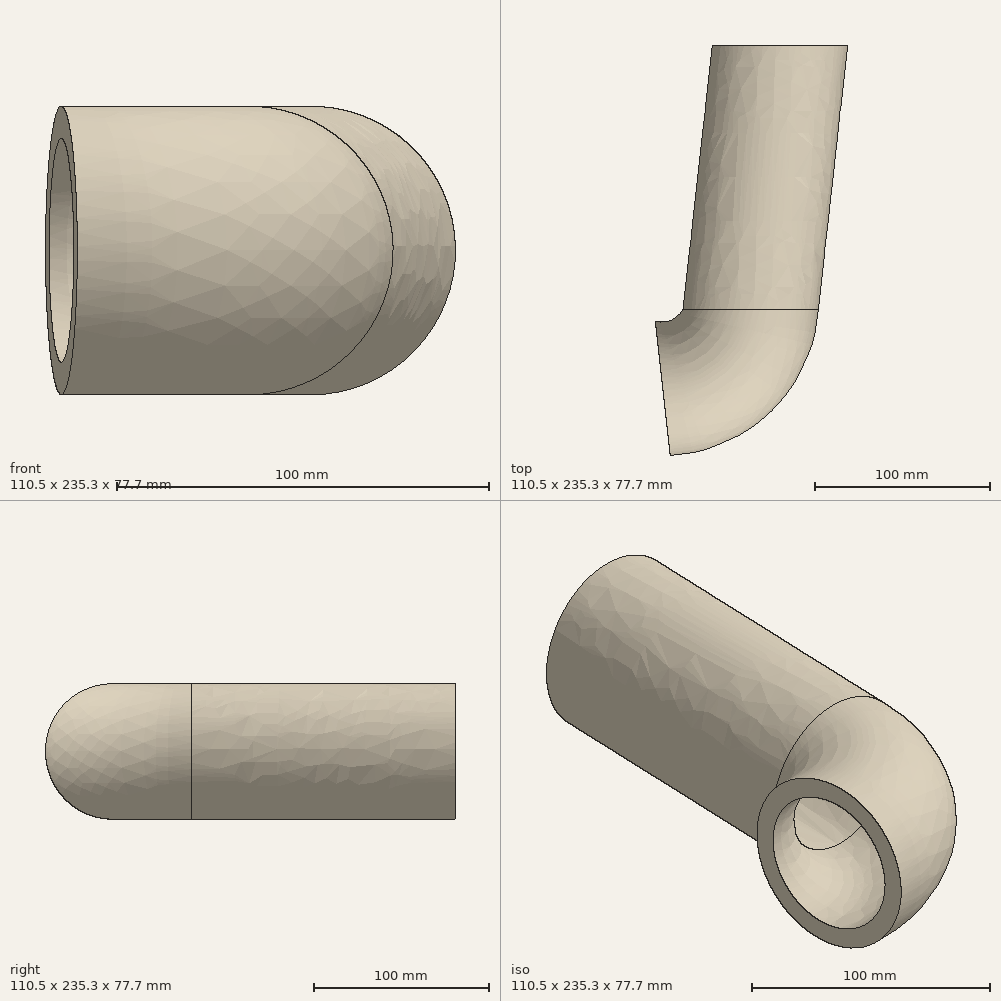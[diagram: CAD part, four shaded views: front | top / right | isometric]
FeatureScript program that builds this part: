
annotation { "Feature Type Name" : "Feature", "Feature Type Description" : "" }
export const myFeature = defineFeature(function(context is Context, id is Id, definition is map)
    precondition{}
    {
        {
            var Q0;
            Q0=qCreatedBy(makeId("Front.planeOp"),FACE);
            var sketch = newSketch(context, id + "F0", { "sketchPlane" : qUnion([Q0])});
            skCircle(sketch, "E0", {"center": v(0, 0) * mm, "radius": 30.16 * mm});
            skCircle(sketch, "E1.0", {"center": v(0, 0) * mm, "radius": 38.87 * mm});
            skSolve(sketch);
        }
        {
            var Q0;
            Q0=qCreatedBy(makeId("Top.planeOp"),FACE);
            var sketch = newSketch(context, id + "F1", { "sketchPlane" : qUnion([Q0])});
            skLineSegment(sketch, "E2", {"start": v(0, 0) * mm, "end": v(-16.82, -151.47) * mm});
            skLineSegment(sketch, "E3", {"start": v(-16.82, -151.47) * mm, "end": v(-67.3, -145.86) * mm, "construction": true});
            skArc(sketch, "E4", {"start": v(-16.82, -151.47) * mm, "mid": v(-33.42, -183.71) * mm, "end": v(-67.3, -196.66) * mm});
            skSolve(sketch);
        }
        {
            var Q0;
            Q0=makeQuery(id+"F0.imprint","IMPRINT",FACE,{"disambiguationData":[TD([[makeQuery(id+"F0.imprint","IMPRINT",EDGE,{"derivedFrom":sQuery(id+"F0.wireOp",EDGE,"E0")}),-1.0]])]});
            var Q1;
            Q1=sQuery(id+"F1.wireOp",EDGE,"E4");
            var Q2;
            Q2=sQuery(id+"F1.wireOp",EDGE,"E2");
            sweep(context, id + "F2", {"profiles" : qUnion([Q0]), "path" : qUnion([Q1, Q2])});
        }
    });
